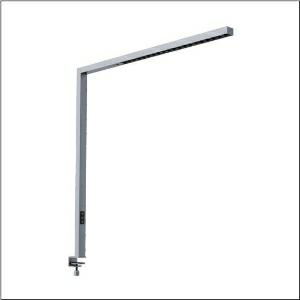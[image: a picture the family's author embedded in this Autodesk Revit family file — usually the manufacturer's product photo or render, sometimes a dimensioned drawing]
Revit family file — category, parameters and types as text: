
# Revit family: silica_31_desk_51my52ga4cs
name_source: partatom
category: Lighting Fixtures
units: mm (PartAtom-declared; Revit-internal decimal feet)

## family parameters
Cut with Voids When Loaded = No
Host = Face
Light Source = No
Part Type = Normal
Room Calculation Point = No
Round Connector Dimension = Use Diameter
Shared = No

## types (1)
- Silica 31 Desk (1 x LED, 10600 lm, 75 W, 4000K)
    Apparent Load = 75 VA
    CIE Flux Codes = 86 100 100 24 100
    Color Rendering = 80
    Color Temperature = 4000K
    Default Elevation = 1800 mm
    Description = Silica® 31 Desk, desktop luminaire, secondary optical cover: cover panel, of PMMA, light emission: direct/indirect distribution, primary light characteristic: symmetric, installation type: as desk luminaire, LED, rated luminous flux: 10.600lm, luminous efficacy: 141lm/W, light colour: 840, colour temperature: 4000K, control gear: Touchdim, daylight-dependent control, with cable with plug, mains connection: 230V, AC, 50Hz, connection cable included, cable length: 2,5m, rated input power: 75W, luminaire head, of aluminium, metallic grey (RAL 9006), length: 1.203mm, width: 52mm, supporting column, angular, of aluminium, metallic grey (RAL 9006), baseplate, of steel, metallic grey (RAL 9006), local control - self-sufficient standalone sensors, direct and indirect component separately switchable, protection rating (complete): IP20, insulation class (complete): insulation class I (protective earthing), certification: CE, ENEC, permissible operating ambient temperature: -20..+40°C, standard: EN 50419, packaging unit: 1 piece
    Height = 36 mm
    Lamp = 1 x LED
    Lamp Light Flux = 10600 lm
    Lamp Power = 75 W
    Lamp count = 1
    Length = 1203 mm
    Luminous efficacy = 141 lm/W
    Manufacturer = Siteco
    ModVariant = No
    Model = 51MY52GA4CS
    Mounting Place = Floor
    Mounting Type = Freestanding
    Number of Poles = 1
    OnlyDefault = Yes
    Power Factor = 1
    Product Name = Silica 31 Desk
    Product group = desktop luminaire
    ProductGroupID = 1303
    Protection Class = Protection class I
    Protection Degree = IP 20
    RLX_Detail_Level = 1
    RLX_Emergency_Light_Flux = 0 lm
    RLX_Emergency_Type = 0
    RLX_Emergency_Type_DB = No
    RlxData = <blob elided: 19793 chars, md5=5a72f3e5>
    Socket = socket
    Standby Power = 0 W
    System Light Flux = 10600 lm
    System Power = 75 W
    Type Comments = Product without accessories
    Type Image = l_1275333.jpg
    URL = http://relux.com
    VarID = ---
    Voltage = 0 V
    Weight = 0.00 kg
    Width = 52 mm  [stored 0.170604 ft]

note: [stored X ft] marks values corroborated as IEEE doubles in the binary element streams (Revit-internal decimal feet)

## geometry (parser evidence)
native form markers: Blend x4, Sweep x17
no freeform markers — native parametric forms only
